# Revit family: VFB_VFB Plus 76-215mm
name_source: partatom
category: Specialty Equipment
revit_build: Autodesk Revit 2015 (Build: 20160512_0715(x64)
units: mm (PartAtom-declared; Revit-internal decimal feet)

## types (140) — shared parameters
Depth = 75 mm
Description = Firefly 102 Ventilated Fire Barrier
IFC Classification = Building Element Proxy
Length = 1000 mm
Manufacturer = Tenmat ltd
Material/Grade = Firefly 102
Performance = BS EN 1366-3:2009 & BS 476, ETA-12/0332, 1224-CPR-0341, CE Marked
URL = https://www.tenmat.com
Youtube Clip = https://www.youtube.com

## per-type parameters (varying)
| type | Seal Type | Tenmat Item Number | Width |
| VFB Plus 76.0 x 75.0 x 1000mm | VFB Plus 120 | I102MP07600075100000
I102MP01600075100000 | 76 mm  [stored 0.249344 ft] |
| VFB Plus 77.0 x 75.0 x 1000mm | VFB Plus 121 | I102MP07700075100000
I102MP01600075100000 | 77 mm  [stored 0.252625 ft] |
| VFB Plus 78.0 x 75.0 x 1000mm | VFB Plus 122 | I102MP07800075100000
I102MP01600075100000 | 78 mm  [stored 0.255906 ft] |
| VFB Plus 79.0 x 75.0 x 1000mm | VFB Plus 123 | I102MP07900075100000
I102MP01600075100000 | 79 mm |
| VFB Plus 80.0 x 75.0 x 1000mm | VFB Plus 124 | I102MP08000075100000
I102MP01600075100000 | 80 mm  [stored 0.262467 ft] |
| VFB Plus 81.0 x 75.0 x 1000mm | VFB Plus 125 | I102MP08100075100000
I102MP01600075100000 | 81 mm  [stored 0.265748 ft] |
| VFB Plus 82.0 x 75.0 x 1000mm | VFB Plus 126 | I102MP08200075100000
I102MP01600075100000 | 82 mm  [stored 0.269029 ft] |
| VFB Plus 83.0 x 75.0 x 1000mm | VFB Plus 127 | I102MP08300075100000
I102MP01600075100000 | 83 mm  [stored 0.27231 ft] |
| VFB Plus 84.0 x 75.0 x 1000mm | VFB Plus 128 | I102MP08400075100000
I102MP01600075100000 | 84 mm  [stored 0.275591 ft] |
| VFB Plus 85.0 x 75.0 x 1000mm | VFB Plus 129 | I102MP08500075100000
I102MP01600075100000 | 85 mm  [stored 0.278871 ft] |
| VFB Plus 86.0 x 75.0 x 1000mm | VFB Plus 130 | I102MP08600075100000
I102MP01600075100000 | 86 mm  [stored 0.282152 ft] |
| VFB Plus 87.0 x 75.0 x 1000mm | VFB Plus 131 | I102MP08700075100000
I102MP01600075100000 | 87 mm  [stored 0.285433 ft] |
| VFB Plus 88.0 x 75.0 x 1000mm | VFB Plus 132 | I102MP08800075100000
I102MP01600075100000 | 88 mm  [stored 0.288714 ft] |
| VFB Plus 89.0 x 75.0 x 1000mm | VFB Plus 133 | I102MP08900075100000
I102MP01600075100000 | 89 mm  [stored 0.291995 ft] |
| VFB Plus 90.0 x 75.0 x 1000mm | VFB Plus 134 | I102MP09000075100000
I102MP01600075100000 | 90 mm  [stored 0.295276 ft] |
| VFB Plus 91.0 x 75.0 x 1000mm | VFB Plus 135 | I102MP09100075100000
I102MP01600075100000 | 91 mm  [stored 0.298556 ft] |
| VFB Plus 92.0 x 75.0 x 1000mm | VFB Plus 136 | I102MP09200075100000
I102MP01600075100000 | 92 mm  [stored 0.301837 ft] |
| VFB Plus 93.0 x 75.0 x 1000mm | VFB Plus 137 | I102MP09300075100000
I102MP01600075100000 | 93 mm  [stored 0.305118 ft] |
| VFB Plus 94.0 x 75.0 x 1000mm | VFB Plus 138 | I102MP09400075100000
I102MP01600075100000 | 94 mm  [stored 0.308399 ft] |
| VFB Plus 95.0 x 75.0 x 1000mm | VFB Plus 139 | I102MP09500075100000
I102MP01600075100000 | 95 mm |
| VFB Plus 96.0 x 75.0 x 1000mm | VFB Plus 140 | I102MP09600075100000
I102MP01600075100000 | 96 mm  [stored 0.314961 ft] |
| VFB Plus 97.0 x 75.0 x 1000mm | VFB Plus 141 | I102MP09700075100000
I102MP01600075100000 | 97 mm  [stored 0.318241 ft] |
| VFB Plus 98.0 x 75.0 x 1000mm | VFB Plus 142 | I102MP09800075100000
I102MP01600075100000 | 98 mm  [stored 0.321522 ft] |
| VFB Plus 99.0 x 75.0 x 1000mm | VFB Plus 143 | I102MP09900075100000
I102MP01600075100000 | 99 mm  [stored 0.324803 ft] |
| VFB Plus 100.0 x 75.0 x 1000mm | VFB Plus 144 | I102MP10000075100000
I102MP01600075100000 | 100 mm  [stored 0.328084 ft] |
| VFB Plus 101.0 x 75.0 x 1000mm | VFB Plus 145 | I102MP10100075100000 | 101 mm  [stored 0.331365 ft] |
| VFB Plus 102.0 x 75.0 x 1000mm | VFB Plus 146 | I102MP10200075100000 | 102 mm |
| VFB Plus 103.0 x 75.0 x 1000mm | VFB Plus 147 | I102MP10300075100000 | 103 mm  [stored 0.337927 ft] |
| VFB Plus 104.0 x 75.0 x 1000mm | VFB Plus 148 | I102MP10400075100000 | 104 mm |
| VFB Plus 105.0 x 75.0 x 1000mm | VFB Plus 149 | I102MP10500075100000 | 105 mm  [stored 0.344488 ft] |
| VFB Plus 106.0 x 75.0 x 1000mm | VFB Plus 150 | I102MP10600075100000 | 106 mm  [stored 0.347769 ft] |
| VFB Plus 107.0 x 75.0 x 1000mm | VFB Plus 151 | I102MP10700075100000 | 107 mm  [stored 0.35105 ft] |
| VFB Plus 108.0 x 75.0 x 1000mm | VFB Plus 152 | I102MP10800075100000 | 108 mm  [stored 0.354331 ft] |
| VFB Plus 109.0 x 75.0 x 1000mm | VFB Plus 153 | I102MP10900075100000 | 109 mm  [stored 0.357612 ft] |
| VFB Plus 110.0 x 75.0 x 1000mm | VFB Plus 154 | I102MP11000075100000 | 110 mm  [stored 0.360892 ft] |
| VFB Plus 111.0 x 75.0 x 1000mm | VFB Plus 155 | I102MP11100075100000 | 111 mm |
| VFB Plus 112.0 x 75.0 x 1000mm | VFB Plus 156 | I102MP11200075100000 | 112 mm  [stored 0.367454 ft] |
| VFB Plus 113.0 x 75.0 x 1000mm | VFB Plus 157 | I102MP11300075100000 | 113 mm  [stored 0.370735 ft] |
| VFB Plus 114.0 x 75.0 x 1000mm | VFB Plus 158 | I102MP11400075100000 | 114 mm  [stored 0.374016 ft] |
| VFB Plus 115.0 x 75.0 x 1000mm | VFB Plus 159 | I102MP11500075100000 | 115 mm |
| VFB Plus 116.0 x 75.0 x 1000mm | VFB Plus 160 | I102MP11600075100000 | 116 mm |
| VFB Plus 117.0 x 75.0 x 1000mm | VFB Plus 161 | I102MP11700075100000 | 117 mm |
| VFB Plus 118.0 x 75.0 x 1000mm | VFB Plus 162 | I102MP11800075100000 | 118 mm |
| VFB Plus 119.0 x 75.0 x 1000mm | VFB Plus 163 | I102MP11900075100000
I102MP01600075100000 | 119 mm |
| VFB Plus 120.0 x 75.0 x 1000mm | VFB Plus 164 | I102MP12000075100000 | 120 mm |
| VFB Plus 121.0 x 75.0 x 1000mm | VFB Plus 165 | I102MP12100075100000 | 121 mm |
| VFB Plus 122.0 x 75.0 x 1000mm | VFB Plus 166 | I102MP12200075100000 | 122 mm |
| VFB Plus 123.0 x 75.0 x 1000mm | VFB Plus 167 | I102MP12300075100000 | 123 mm |
| VFB Plus 124.0 x 75.0 x 1000mm | VFB Plus 168 | I102MP12400075100000 | 124 mm |
| VFB Plus 125.0 x 75.0 x 1000mm | VFB Plus 169 | I102MP12500075100000 | 125 mm |
| VFB Plus 126.0 x 75.0 x 1000mm | VFB Plus 170 | I102MP07500075100000
I102MP12600075100000 | 126 mm |
| VFB Plus 127.0 x 75.0 x 1000mm | VFB Plus 171 | I102MP12700075100000 | 127 mm |
| VFB Plus 128.0 x 75.0 x 1000mm | VFB Plus 172 | I102MP12800075100000 | 128 mm |
| VFB Plus 129.0 x 75.0 x 1000mm | VFB Plus 173 | I102MP12900075100000 | 129 mm |
| VFB Plus 130.0 x 75.0 x 1000mm | VFB Plus 174 | I102MP07500075100000
I102MP13000075100000 | 130 mm |
| VFB Plus 131.0 x 75.0 x 1000mm | VFB Plus 175 | I102MP07500075100000
I102MP13100075100000 | 131 mm |
| VFB Plus 132.0 x 75.0 x 1000mm | VFB Plus 176 | I102MP07500075100000
I102MP13200075100000 | 132 mm |
| VFB Plus 133.0 x 75.0 x 1000mm | VFB Plus 177 | I102MP07500075100000
I102MP13300075100000 | 133 mm |
| VFB Plus 134.0 x 75.0 x 1000mm | VFB Plus 178 | I102MP07500075100000
I102MP13400075100000 | 134 mm |
| VFB Plus 135.0 x 75.0 x 1000mm | VFB Plus 179 | I102MP07500075100000
I102MP13500075100000 | 135 mm |
| VFB Plus 136.0 x 75.0 x 1000mm | VFB Plus 180 | I102MP07500075100000
I102MP13600075100000 | 136 mm |
| VFB Plus 137.0 x 75.0 x 1000mm | VFB Plus 181 | I102MP07500075100000
I102MP13700075100000 | 137 mm |
| VFB Plus 138.0 x 75.0 x 1000mm | VFB Plus 182 | I102MP07500075100000
I102MP13800075100000 | 138 mm |
| VFB Plus 139.0 x 75.0 x 1000mm | VFB Plus 183 | I102MP07500075100000
I102MP13900075100000 | 139 mm |
| VFB Plus 140.0 x 75.0 x 1000mm | VFB Plus 184 | I102MP07500075100000
I102MP14000075100000
I102MP01600075100000 | 140 mm |
| VFB Plus 141.0 x 75.0 x 1000mm | VFB Plus 185 | I102MP14100075100000 | 141 mm |
| VFB Plus 142.0 x 75.0 x 1000mm | VFB Plus 186 | I102MP14200075100000 | 142 mm |
| VFB Plus 143.0 x 75.0 x 1000mm | VFB Plus 187 | I102MP14300075100000 | 143 mm |
| VFB Plus 144.0 x 75.0 x 1000mm | VFB Plus 188 | I102MP14400075100000 | 144 mm |
| VFB Plus 145.0 x 75.0 x 1000mm | VFB Plus 189 | I102MP14500075100000 | 145 mm |
| VFB Plus 146.0 x 75.0 x 1000mm | VFB Plus 190 | I102MP07500075100000
I102MP14600075100000 | 146 mm |
| VFB Plus 147.0 x 75.0 x 1000mm | VFB Plus 191 | I102MP14700075100000 | 147 mm |
| VFB Plus 148.0 x 75.0 x 1000mm | VFB Plus 192 | I102MP14800075100000 | 148 mm |
| VFB Plus 149.0 x 75.0 x 1000mm | VFB Plus 193 | I102MP14900075100000 | 149 mm |
| VFB Plus 150.0 x 75.0 x 1000mm | VFB Plus 194 | I102MP15000075100000 | 150 mm |
| VFB Plus 151.0 x 75.0 x 1000mm | VFB Plus 195 | I102MP15100075100000 | 151 mm |
| VFB Plus 152.0 x 75.0 x 1000mm | VFB Plus 196 | I102MP15200075100000 | 152 mm |
| VFB Plus 153.0 x 75.0 x 1000mm | VFB Plus 197 | I102MP15300075100000 | 153 mm |
| VFB Plus 154.0 x 75.0 x 1000mm | VFB Plus 198 | I102MP15400075100000 | 154 mm |
| VFB Plus 155.0 x 75.0 x 1000mm | VFB Plus 199 | I102MP15500075100000 | 155 mm |
| VFB Plus 156.0 x 75.0 x 1000mm | VFB Plus 200 | I102MP15600075100000 | 156 mm |
| VFB Plus 157.0 x 75.0 x 1000mm | VFB Plus 201 | I102MP15700075100000 | 157 mm |
| VFB Plus 158.0 x 75.0 x 1000mm | VFB Plus 202 | I102MP15800075100000 | 158 mm |
| VFB Plus 159.0 x 75.0 x 1000mm | VFB Plus 203 | I102MP15900075100000 | 159 mm |
| VFB Plus 160.0 x 75.0 x 1000mm | VFB Plus 204 | I102MP16000075100000 | 160 mm |
| VFB Plus 161.0 x 75.0 x 1000mm | VFB Plus 205 | I102MP16100075100000 | 161 mm |
| VFB Plus 162.0 x 75.0 x 1000mm | VFB Plus 206 | I102MP16000075100000
I102MP16200075100000 | 162 mm |
| VFB Plus 163.0 x 75.0 x 1000mm | VFB Plus 207 | I102MP16300075100000 | 163 mm |
| VFB Plus 164.0 x 75.0 x 1000mm | VFB Plus 208 | I102MP16400075100000 | 164 mm |
| VFB Plus 165.0 x 75.0 x 1000mm | VFB Plus 209 | I102MP16500075100000 | 165 mm |
| VFB Plus 166.0 x 75.0 x 1000mm | VFB Plus 210 | I102MP16600075100000 | 166 mm |
| VFB Plus 167.0 x 75.0 x 1000mm | VFB Plus 211 | I102MP16700075100000 | 167 mm |
| VFB Plus 168.0 x 75.0 x 1000mm | VFB Plus 212 | I102MP16800075100000 | 168 mm |
| VFB Plus 169.0 x 75.0 x 1000mm | VFB Plus 213 | I102MP16900075100000 | 169 mm |
| VFB Plus 170.0 x 75.0 x 1000mm | VFB Plus 214 | I102MP17000075100000 | 170 mm |
| VFB Plus 171.0 x 75.0 x 1000mm | VFB Plus 215 | I102MP17100075100000 | 171 mm |
| VFB Plus 172.0 x 75.0 x 1000mm | VFB Plus 216 | I102MP17200075100000 | 172 mm |
| VFB Plus 173.0 x 75.0 x 1000mm | VFB Plus 217 | I102MP17300075100000 | 173 mm |
| VFB Plus 174.0 x 75.0 x 1000mm | VFB Plus 218 | I102MP17400075100000 | 174 mm |
| VFB Plus 175.0 x 75.0 x 1000mm | VFB Plus 219 | I102MP17500075100000 | 175 mm |
| VFB Plus 176.0 x 75.0 x 1000mm | VFB Plus 220 | I102MP17600075100000 | 176 mm |
| VFB Plus 177.0 x 75.0 x 1000mm | VFB Plus 221 | I102MP17700075100000 | 177 mm |
| VFB Plus 178.0 x 75.0 x 1000mm | VFB Plus 222 | I102MP17800075100000 | 178 mm |
| VFB Plus 179.0 x 75.0 x 1000mm | VFB Plus 223 | I102MP17900075100000 | 179 mm |
| VFB Plus 180.0 x 75.0 x 1000mm | VFB Plus 224 | I102MP18000075100000 | 180 mm |
| VFB Plus 181.0 x 75.0 x 1000mm | VFB Plus 225 | I102MP18100075100000 | 181 mm |
| VFB Plus 182.0 x 75.0 x 1000mm | VFB Plus 226 | I102MP18200075100000 | 182 mm |
| VFB Plus 183.0 x 75.0 x 1000mm | VFB Plus 227 | I102MP18300075100000 | 183 mm |
| VFB Plus 184.0 x 75.0 x 1000mm | VFB Plus 228 | I102MP18400075100000 | 184 mm |
| VFB Plus 185.0 x 75.0 x 1000mm | VFB Plus 229 | I102MP18500075100000 | 185 mm |
| VFB Plus 186.0 x 75.0 x 1000mm | VFB Plus 230 | I102MP18600075100000 | 186 mm |
| VFB Plus 187.0 x 75.0 x 1000mm | VFB Plus 231 | I102MP18700075100000 | 187 mm |
| VFB Plus 188.0 x 75.0 x 1000mm | VFB Plus 232 | I102MP18800075100000 | 188 mm |
| VFB Plus 189.0 x 75.0 x 1000mm | VFB Plus 233 | I102MP18900075100000 | 189 mm |
| VFB Plus 190.0 x 75.0 x 1000mm | VFB Plus 234 | I102MP19000075100000 | 190 mm |
| VFB Plus 191.0 x 75.0 x 1000mm | VFB Plus 235 | I102MP19100075100000 | 191 mm |
| VFB Plus 192.0 x 75.0 x 1000mm | VFB Plus 236 | I102MP19200075100000 | 192 mm |
| VFB Plus 193.0 x 75.0 x 1000mm | VFB Plus 237 | I102MP19300075100000 | 193 mm |
| VFB Plus 194.0 x 75.0 x 1000mm | VFB Plus 238 | I102MP19400075100000 | 194 mm |
| VFB Plus 195.0 x 75.0 x 1000mm | VFB Plus 239 | I102MP19500075100000 | 195 mm |
| VFB Plus 196.0 x 75.0 x 1000mm | VFB Plus 240 | I102MP19600075100000 | 196 mm |
| VFB Plus 197.0 x 75.0 x 1000mm | VFB Plus 241 | I102MP19700075100000 | 197 mm |
| VFB Plus 198.0 x 75.0 x 1000mm | VFB Plus 242 | I102MP19800075100000 | 198 mm |
| VFB Plus 199.0 x 75.0 x 1000mm | VFB Plus 243 | I102MP19900075100000 | 199 mm |
| VFB Plus 200.0 x 75.0 x 1000mm | VFB Plus 244 | I102MP20000075100000 | 200 mm |
| VFB Plus 201.0 x 75.0 x 1000mm | VFB Plus 245 | I102MP20100075100000 | 201 mm |
| VFB Plus 202.0 x 75.0 x 1000mm | VFB Plus 246 | I102MP20200075100000 | 202 mm |
| VFB Plus 203.0 x 75.0 x 1000mm | VFB Plus 247 | I102MP20300075100000 | 203 mm |
| VFB Plus 204.0 x 75.0 x 1000mm | VFB Plus 248 | I102MP20400075100000 | 204 mm |
| VFB Plus 205.0 x 75.0 x 1000mm | VFB Plus 249 | I102MP20500075100000 | 205 mm |
| VFB Plus 206.0 x 75.0 x 1000mm | VFB Plus 250 | I102MP20600075100000 | 206 mm |
| VFB Plus 207.0 x 75.0 x 1000mm | VFB Plus 251 | I102MP20700075100000 | 207 mm |
| VFB Plus 208.0 x 75.0 x 1000mm | VFB Plus 252 | I102MP20800075100000 | 208 mm |
| VFB Plus 209.0 x 75.0 x 1000mm | VFB Plus 253 | I102MP20900075100000 | 209 mm |
| VFB Plus 210.0 x 75.0 x 1000mm | VFB Plus 254 | I102MP21000075100000 | 210 mm |
| VFB Plus 211.0 x 75.0 x 1000mm | VFB Plus 255 | I102MP21100075100000 | 211 mm |
| VFB Plus 212.0 x 75.0 x 1000mm | VFB Plus 256 | I102MP21200075100000 | 212 mm |
| VFB Plus 213.0 x 75.0 x 1000mm | VFB Plus 257 | I102MP21300075100000 | 213 mm |
| VFB Plus 214.0 x 75.0 x 1000mm | VFB Plus 258 | I102MP21400075100000 | 214 mm |
| VFB Plus 215.0 x 75.0 x 1000mm | VFB Plus 259 | I102MP21500075100000 | 215 mm |

note: [stored X ft] marks values corroborated as IEEE doubles in the binary element streams (Revit-internal decimal feet)

## geometry (parser evidence)
native form markers: Blend x2, Sweep x5
no freeform markers — native parametric forms only
